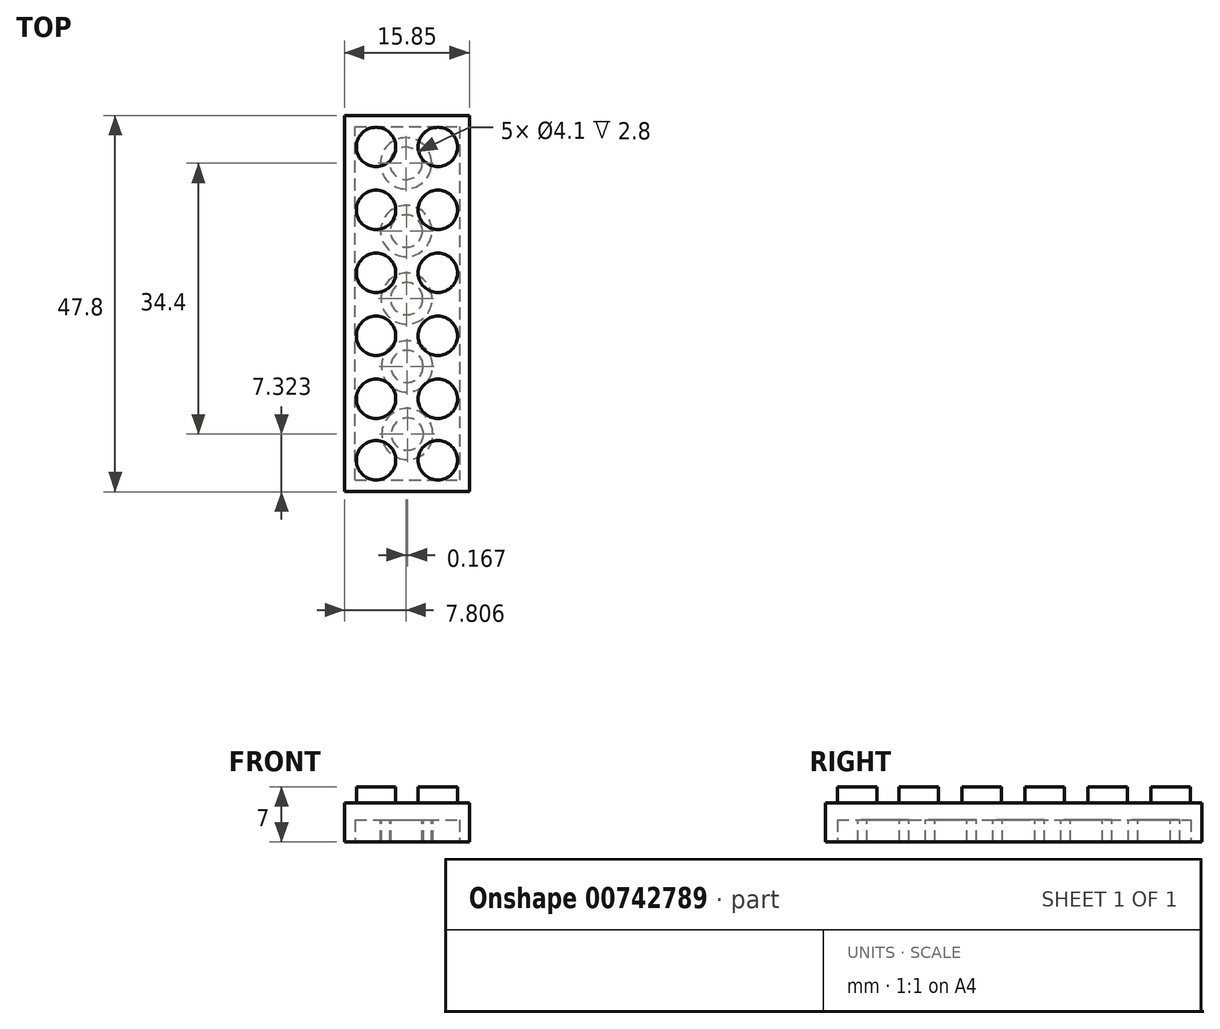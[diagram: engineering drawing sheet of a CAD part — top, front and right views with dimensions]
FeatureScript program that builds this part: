
annotation { "Feature Type Name" : "Feature", "Feature Type Description" : "" }
export const myFeature = defineFeature(function(context is Context, id is Id, definition is map)
    precondition{}
    {
        {
            var Q0;
            Q0=qCreatedBy(makeId("Top.planeOp"),FACE);
            var sketch = newSketch(context, id + "F0", { "sketchPlane" : qUnion([Q0])});
            skLineSegment(sketch, "E0", {"start": v(-52.83, 62.4) * mm, "end": v(-52.83, 14.6) * mm});
            skLineSegment(sketch, "E1", {"start": v(-52.83, 62.4) * mm, "end": v(-36.98, 62.4) * mm});
            skLineSegment(sketch, "E2", {"start": v(-36.98, 14.6) * mm, "end": v(-36.98, 62.4) * mm});
            skLineSegment(sketch, "E3", {"start": v(-36.98, 14.6) * mm, "end": v(-52.83, 14.6) * mm});
            skSolve(sketch);
        }
        {
            var Q0;
            Q0 = qSketchRegion(id + "F0", true);
            extrude(context, id + "F1", {"entities" : qUnion([Q0]), "depth" : 5 * mm, "offsetDistance" : 25 * mm});
        }
        {
            var Q0;
            Q0=makeQuery(id+"F1.opExtrude","CAP_FACE",FACE,{"disambiguationData":[OSD([sQuery(id+"F0.wireOp",EDGE,"E0"),sQuery(id+"F0.wireOp",EDGE,"E1"),sQuery(id+"F0.wireOp",EDGE,"E2"),sQuery(id+"F0.wireOp",EDGE,"E3")])],"isStart":false});
            var sketch = newSketch(context, id + "F2", { "sketchPlane" : qUnion([Q0])});
            skCircle(sketch, "E4", {"center": v(-48.83, 58.4) * mm, "radius": 2.5 * mm});
            skCircle(sketch, "E5", {"center": v(-40.98, 58.4) * mm, "radius": 2.5 * mm});
            skCircle(sketch, "E6", {"center": v(-48.83, 18.6) * mm, "radius": 2.5 * mm});
            skCircle(sketch, "E7", {"center": v(-40.98, 18.6) * mm, "radius": 2.5 * mm});
            skCircle(sketch, "E8", {"center": v(-48.83, 50.4) * mm, "radius": 2.5 * mm});
            skCircle(sketch, "E9", {"center": v(-40.98, 50.4) * mm, "radius": 2.5 * mm});
            skCircle(sketch, "E10", {"center": v(-48.83, 26.4) * mm, "radius": 2.5 * mm});
            skCircle(sketch, "E11", {"center": v(-40.98, 26.4) * mm, "radius": 2.5 * mm});
            skCircle(sketch, "E12", {"center": v(-48.83, 42.4) * mm, "radius": 2.5 * mm});
            skCircle(sketch, "E13", {"center": v(-40.98, 42.4) * mm, "radius": 2.5 * mm});
            skCircle(sketch, "E14", {"center": v(-48.83, 34.4) * mm, "radius": 2.5 * mm});
            skCircle(sketch, "E15", {"center": v(-40.98, 34.4) * mm, "radius": 2.5 * mm});
            skSolve(sketch);
        }
        {
            var Q0;
            Q0 = qSketchRegion(id + "F2", true);
            extrude(context, id + "F3", {"entities" : qUnion([Q0]), "operationType" : NewBodyOperationType.ADD, "depth" : 2 * mm, "offsetDistance" : 25 * mm});
        }
        {
            var Q0;
            Q0=makeQuery(id+"F1.opExtrude","CAP_FACE",FACE,{"disambiguationData":[OSD([sQuery(id+"F0.wireOp",EDGE,"E0"),sQuery(id+"F0.wireOp",EDGE,"E1"),sQuery(id+"F0.wireOp",EDGE,"E2"),sQuery(id+"F0.wireOp",EDGE,"E3")])],"isStart":true});
            var sketch = newSketch(context, id + "F4", { "sketchPlane" : qUnion([Q0])});
            skLineSegment(sketch, "E16", {"start": v(-51.52, -16.07) * mm, "end": v(-38.2, -16.07) * mm});
            skLineSegment(sketch, "E17", {"start": v(-51.52, -16.07) * mm, "end": v(-51.52, -60.97) * mm});
            skLineSegment(sketch, "E18", {"start": v(-51.52, -60.97) * mm, "end": v(-38.2, -60.97) * mm});
            skLineSegment(sketch, "E19", {"start": v(-38.2, -60.97) * mm, "end": v(-38.2, -16.07) * mm});
            skSolve(sketch);
        }
        {
            var Q0;
            Q0 = qSketchRegion(id + "F4", true);
            extrude(context, id + "F5", {"entities" : qUnion([Q0]), "operationType" : NewBodyOperationType.REMOVE, "oppositeDirection" : true, "depth" : 2.8 * mm, "offsetDistance" : 25 * mm});
        }
        {
            var Q0;
            Q0=makeQuery(id+"F5.boolean.opBoolean","COPY",FACE,{"derivedFrom":makeQuery(id+"F5.opExtrude","CAP_FACE",FACE,{"disambiguationData":[OSD([sQuery(id+"F4.wireOp",EDGE,"E16"),sQuery(id+"F4.wireOp",EDGE,"E17"),sQuery(id+"F4.wireOp",EDGE,"E18"),sQuery(id+"F4.wireOp",EDGE,"E19")])],"isStart":false})});
            var sketch = newSketch(context, id + "F6", { "sketchPlane" : qUnion([Q0])});
            skLineSegment(sketch, "E20", {"start": v(-44.86, -16.07) * mm, "end": v(-44.86, -60.97) * mm});
            skCircle(sketch, "E21", {"center": v(-44.86, -21.92) * mm, "radius": 3.25 * mm});
            skCircle(sketch, "E22.1.0.0", {"center": v(-44.9, -30.52) * mm, "radius": 3.25 * mm});
            skCircle(sketch, "E22.2.0.0", {"center": v(-44.95, -39.12) * mm, "radius": 3.25 * mm});
            skCircle(sketch, "E22.3.0.0", {"center": v(-44.99, -47.72) * mm, "radius": 3.25 * mm});
            skCircle(sketch, "E22.4.0.0", {"center": v(-45.03, -56.32) * mm, "radius": 3.25 * mm});
            skLineSegment(sketch, "E22.direction1", {"start": v(-44.86, -21.92) * mm, "end": v(-44.9, -30.52) * mm, "construction": true});
            skCircle(sketch, "E23", {"center": v(-44.86, -21.92) * mm, "radius": 2.05 * mm});
            skCircle(sketch, "E24.1.0.0", {"center": v(-44.9, -30.52) * mm, "radius": 2.05 * mm});
            skCircle(sketch, "E24.2.0.0", {"center": v(-44.94, -39.12) * mm, "radius": 2.05 * mm});
            skCircle(sketch, "E24.3.0.0", {"center": v(-44.98, -47.72) * mm, "radius": 2.05 * mm});
            skCircle(sketch, "E24.4.0.0", {"center": v(-45.02, -56.32) * mm, "radius": 2.05 * mm});
            skSolve(sketch);
        }
        {
            var Q0;
            Q0 = qSketchRegion(id + "F6", true);
            extrude(context, id + "F7", {"entities" : qUnion([Q0]), "operationType" : NewBodyOperationType.ADD, "depth" : 2.8 * mm, "offsetDistance" : 25 * mm});
        }
    });
